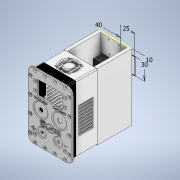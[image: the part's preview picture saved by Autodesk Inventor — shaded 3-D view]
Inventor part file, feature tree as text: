
AUTODESK INVENTOR PART (.ipt)
format: ipt  version: 2022 (Build 260153000, 153)  size: 2,895,872 bytes
history: native  units: in
note: dims shown in document units (in); Inventor stores cm internally (conversion verified against a paired STEP export)
features: sketch x30, extrude x27, fillet x20, other x12, hole x5, chamfer x1
ambient origin geometry x8: Origin, YZ Plane, XZ Plane, XY Plane, X Axis, Y Axis, Z Axis, Center Point
bodies: Body1 (feature_tree), Body2 (feature_tree), Body3 (feature_tree), Body4 (feature_tree), Body5 (feature_tree), Body6 (feature_tree), Body7 (feature_tree), Body8 (feature_tree), Body9 (feature_tree), Body10 (feature_tree), Body11 (feature_tree)
feature tree (95):
  other  "Faceplate"
  extrude  "Front Panel Blank"  Depth=4.7244in
  hole  "Panel Mount Screw Holes"  [1 undecoded]
  extrude  "Voltmeter Screen"  Depth=0.0984in TaperAngle=0.0deg
  extrude  "Knob Indents"  Depth=0.1181in
  extrude  "Pot Mounting Holes"  Depth=0.1181in
  extrude  "Connector Indents"  Depth=0.1181in
  extrude  "Connector Mounting Holes"  Depth=0.1181in
  fillet  "Fillet1"  Radius=0.5906in
  other  "Work Point1"
  extrude  "Pot Back Keepouts"  Depth=1.1811in
  extrude  "Chassis"  Depth=0.5906in
  extrude  "Display"  Depth=0.1969in
  extrude  "Chassis 2"  Depth=1.7717in
  extrude  "Back Chassis Plate"  Depth=0.4724in
  extrude  "PCB Standoffs"  Depth=0.0197in
  extrude  "PCB"  Depth=0.0197in
  hole  "PCB Screw Mounts"  [1 undecoded]
  extrude  "Heatsinks"  Depth=1.063in
  extrude  "Air Holes 1"  Depth=0.7874in
  fillet  "Fillet2"  Radius=0.9449in
  fillet  "Fillet3"  Radius=0.7874in
  extrude  "Fan Body"  Depth=0.6693in
  extrude  "Top Air Holes"  Depth=0.2756in
  hole  "Hole5"  [1 undecoded]
  fillet  "Fillet11"  Radius=0.5512in
  fillet  "Fillet12"  Radius=0.5512in
  fillet  "Fillet13"  Radius=1.378in
  fillet  "Fillet14"  Radius=0.5906in
  extrude  "Text Labels"  Depth=0.0394in
  extrude  "Logo"  TaperAngle=0.0deg  [1 undecoded]
  fillet  "Fillet15"  Radius=0.5906in
  fillet  "Fillet16"  Radius=0.0787in
  fillet  "Fillet17"  Radius=2.3622in
  fillet  "Fillet18"  Radius=1.1811in
  fillet  "Fillet19"  Radius=0.3937in
  fillet  "Fillet20"  Radius=0.5906in
  fillet  "Fillet21"  Radius=1.9685in
  fillet  "Fillet24"  Radius=0.1181in
  fillet  "Fillet25"  Radius=0.1181in
  fillet  "Fillet26"  Radius=0.1181in
  extrude  "Transformer Body"  Depth=0.1181in
  extrude  "Transformer Metal"  Depth=0.2362in
  extrude  "Transformer Yellow"  Depth=0.1181in
  extrude  "body3 lid"  Depth=0.2756in
  extrude  "IEC Panelmount"  Depth=0.3346in
  extrude  "IEC inside"  Depth=0.3346in
  extrude  "IEC socket"  Depth=0.3346in
  extrude  "body3 IEC hole"  Depth=0.7087in
  chamfer  "IEPin Sculpting"  Distance=0.748in
  fillet  "Fillet27"  Radius=0.748in
  fillet  "Fillet28"  Radius=0.3937in
  fillet  "Fillet29"  Radius=0.2756in
  hole  "IEC Screwholes"  [1 undecoded]
  hole  "Faceplate Mounting Holes"  [1 undecoded]
  sketch  "Sketch40"  dims[d153=0.7087in d154=0.7087in d155=0.748in d156=0.748in d157=0.3937in d158=0.0in d160=0.2756in d161=0.315in d164=0.1181in d165=1.1811in d166=0.1181in d167=0.315in d168=0.315in d169=0.2362in d170=0.2362in d171=2.7559in d172=1.1811in d173=0.6693in d174=0.2756in d175=0.1181in d176=0.1181in d177=0.1181in d178=0.1181in d179=0.1181in d180=0.1181in d181=0.1181in d182=0.1181in d183=0.1476in d185=0.5906in d186=0.6299in d187=0.0968in d188=0.2362in d189=0.248in d190=0.0787in d191=90.0deg d192=1.4961in d193=0.8108in d194=0.0787in d195=0.6693in d196=0.0in d197=0.0in d216=1.378in d217=0.0in d218=0.1181in d219=0.0in d220=0.3543in d221=0.3543in d222=0.3543in d223=0.3543in d224=1.0236in d225=2.3031in d226=0.5118in d230=0.1969in d231=0.0in d232=2.5591in d233=1.4567in d234=0.128in d235=0.0886in d236=0.7283in d237=0.063in d238=0.0in d239=0.1181in d240=0.1181in d241=0.1181in d242=0.1181in d243=0.0968in d244=0.2362in d245=0.248in d246=0.0787in d247=90.0deg d248=0.315in d249=0.8108in d250=0.0394in d251=0.1575in d252=0.1575in d253=0.0394in d254=0.0394in d255=0.1575in d256=0.0394in d257=0.1575in d258=0.0394in d259=0.1575in d260=0.0394in d261=0.1575in d262=0.0394in d263=0.1575in d264=0.0394in d265=0.1575in d266=0.0394in d267=0.1575in d268=0.0394in d269=1.811in d270=0.0906in d271=0.3937in d272=0.0906in d274=0.374in d275=0.374in d276=0.8268in d277=0.0in d278=0.1969in d288=1.9685in d289=1.5748in d290=1.1811in d295=0.6693in d296=1.122in d304=0.0984in d305=0.0984in d306=0.0984in d307=0.0984in d308=0.0984in d309=0.0984in d310=0.0984in d311=0.0984in d312=0.0984in d313=0.1181in d314=0.1181in d315=0.1181in d316=0.1181in d317=0.1181in d318=0.1181in d319=0.1181in d320=0.1181in d321=0.315in d322=0.1969in d323=0.0in d324=0.0in d326=0.0689in d327=0.0689in d353=0.3937in d354=0.0in d355=0.0394in d356=0.0787in d357=1.1811in d358=1.1811in d359=0.0787in d360=0.0787in d361=0.0787in d362=0.0787in d363=0.9449in d364=0.9449in d365=0.1181in d366=0.1181in d367=0.1181in d368=0.1181in d375=0.5512in d376=0.0in d377=1.1024in d378=0.5906in d379=0.5906in d380=0.7283in d381=0.0787in d382=0.0787in d383=0.0787in d384=0.0394in d385=0.0394in d386=0.0394in d387=0.0787in d388=0.0787in d389=0.3642in d390=0.5512in d391=0.3642in d392=0.5512in d393=0.3642in d394=0.5512in d395=0.3642in d396=0.5512in d397=0.0787in d398=0.0787in d399=0.0408in d400=0.1877in d401=0.0408in d402=0.0408in d403=0.5906in d404=0.5906in d405=0.0787in d406=0.1181in d441=0.0787in d442=0.0787in d443=0.0787in d444=0.0787in d445=0.0617in d446=0.1575in d447=0.119in d448=0.188in d449=0.5635in d450=0.248in d451=0.0in d452=0.0787in d453=0.0787in d454=0.0394in d455=0.0394in d456=0.1181in d457=0.1181in d459=0.5118in d460=0.2362in d461=0.7087in d463=0.7087in d464=0.7087in d465=0.0787in d466=0.0787in d468=0.4134in d471=1.3386in d472=0.1969in d473=0.5709in d476=0.0787in d477=0.0in d479=0.0787in d480=0.0in d481=0.0in d488=0.0in d489=0.0in d490=0.7382in d491=0.1772in d492=0.1772in d493=0.7382in d494=0.1772in d495=0.1772in d496=0.1772in d497=0.1772in d498=0.5512in d499=0.5512in d500=0.5512in d501=0.6693in d502=0.3642in d503=0.3642in d504=0.187in d505=0.187in d506=0.0984in d507=0.0984in d508=0.0787in d509=0.0787in d510=0.0787in d511=0.0394in d512=0.0118in d513=4.7244in d514=2.3622in d515=0.0in d518=0.0551in d519=0.0551in d520=0.0551in d521=1.5945in d522=0.1476in d531=0.1476in d532=0.5512in d533=1.2205in d534=1.8976in d535=0.0in d536=1.2598in d537=1.1417in d538=0.2264in d539=0.2264in d540=0.3189in d541=0.3189in d542=0.5118in d543=1.6614in d544=0.0in d545=0.0in d546=0.1181in d547=0.0in d549=1.3012in d552=0.6506in d553=1.124in d554=0.3268in d555=0.6506in d556=0.6506in d557=0.3268in d558=0.1969in d559=0.0in d560=1.2205in d561=1.063in d562=0.0394in d564=0.0305in d566=0.5512in d567=0.9843in d568=0.9843in d570=0.2559in d571=0.2362in d572=0.0305in d573=0.2559in d574=0.689in d575=0.0in d576=0.9567in d577=0.6535in d578=0.1205in d579=0.0837in d580=0.0837in d581=0.5402in d582=0.2083in d583=0.2083in d585=0.1969in d586=0.0787in d587=0.0787in d588=0.0787in d589=0.1575in d590=0.1575in d591=0.1575in d592=0.1575in d593=0.3307in d594=0.439in d595=0.439in d596=0.1575in d597=0.1575in d598=0.689in d599=0.0in d600=0.689in d601=0.0in d602=0.0394in d603=0.0787in d604=45.0deg d605=0.1969in d606=0.1181in d607=0.1181in d608=0.2247in d609=0.2247in d611=1.437in d612=0.2402in d613=0.2402in d614=0.6496in d615=0.0968in d616=0.2362in d617=0.1575in d618=0.0787in d619=90.0deg d620=0.315in d621=0.8108in d622=0.9449in d623=0.0394in d624=1.7776in d625=0.3268in d626=0.9843in d627=1.1811in d629=1.5748in d630=0.3937in d631=1.6772in d632=1.6772in d633=1.1417in d634=1.0236in]
  sketch  "Sketch1"  dims[d0=3.1496in d1=4.7244in]
  sketch  "Sketch2"  dims[d2=2.3622in d4=1.5748in]
  sketch  "Sketch3"  dims[d5=0.3937in d6=0.0984in d7=0.0in]
  sketch  "Sketch4"  dims[d8=0.1181in d9=0.1181in]
  sketch  "Sketch5"  dims[d10=0.1181in d11=0.1181in]
  sketch  "Sketch6"  dims[d12=0.1181in d13=0.1181in]
  sketch  "Sketch7"  dims[d14=0.1181in d15=0.1181in d16=0.5906in]
  other  "Body 1"
  sketch  "Sketch11"  dims[d17=0.5906in d18=1.1811in]
  sketch  "Sketch14"  dims[d19=0.5906in d20=0.5906in]
  other  "Pots"
  sketch  "Sketch15"  dims[d21=0.1969in d22=0.1969in]
  other  "Screen"
  sketch  "Sketch16"  dims[d23=0.126in d24=0.2362in d25=0.248in d26=0.0787in d27=90.0deg d28=0.315in d29=0.8108in d30=1.7717in]
  other  "Body 2"
  sketch  "Sketch17"  dims[d31=0.5906in d32=1.0236in d33=0.8858in d34=0.9449in d35=0.4724in]
  sketch  "Sketch18"  dims[d36=0.0197in d37=0.0197in d38=0.0197in]
  other  "Power Module"
  sketch  "Sketch20"  dims[d39=0.0197in d40=0.9449in]
  sketch  "Sketch21"  dims[d42=0.5906in d43=1.0236in]
  other  "Power Moudle Heat Sinks"
  sketch  "Sketch22"  dims[d44=0.4724in d45=1.063in]
  sketch  "Sketch24"  dims[d46=0.1969in d47=0.0in d48=0.9449in d49=0.9449in d50=0.7874in]
  other  "Cooling_fan"
  sketch  "Sketch25"  dims[d51=0.6693in d52=0.6693in]
  sketch  "Sketch26"  dims[d53=0.0394in d54=0.0in d55=0.2756in]
  sketch  "Sketch28"  dims[d56=0.2756in d57=0.0394in d58=0.0in d59=0.5512in d60=0.5512in d61=1.378in d64=0.5906in]
  sketch  "Sketch30"  dims[d65=0.0394in d66=0.0in d67=0.187in]
  other  "Body 3"
  sketch  "Sketch31"  dims[d68=0.187in d69=0.0in d70=0.0in d71=0.5906in d72=0.0787in d81=2.3622in d82=1.1811in d85=0.3937in d86=0.2756in d87=0.5906in d88=0.0in d91=1.9685in d99=0.1181in d100=0.1181in d101=0.1181in]
  other  "Transformer"
  sketch  "Sketch32"  dims[d102=0.1181in d103=0.1181in]
  sketch  "Sketch33"  dims[d104=0.2362in d105=0.2362in]
  sketch  "Sketch34"  dims[d106=0.1181in d109=0.1476in]
  other  "IEC"
  sketch  "Sketch35"  dims[d110=0.2756in d111=0.128in]
  sketch  "Sketch36"  dims[d147=0.6693in d148=0.3346in]
  sketch  "Sketch37"  dims[d149=0.6693in d150=0.3346in]
  sketch  "Sketch39"  dims[d151=0.3346in d152=0.3346in]
note: 6 required parameter values undecoded (feature->parameter linkage not recoverable at this tier; creation-order binding heuristic only, values carry confidence <= 0.55)
